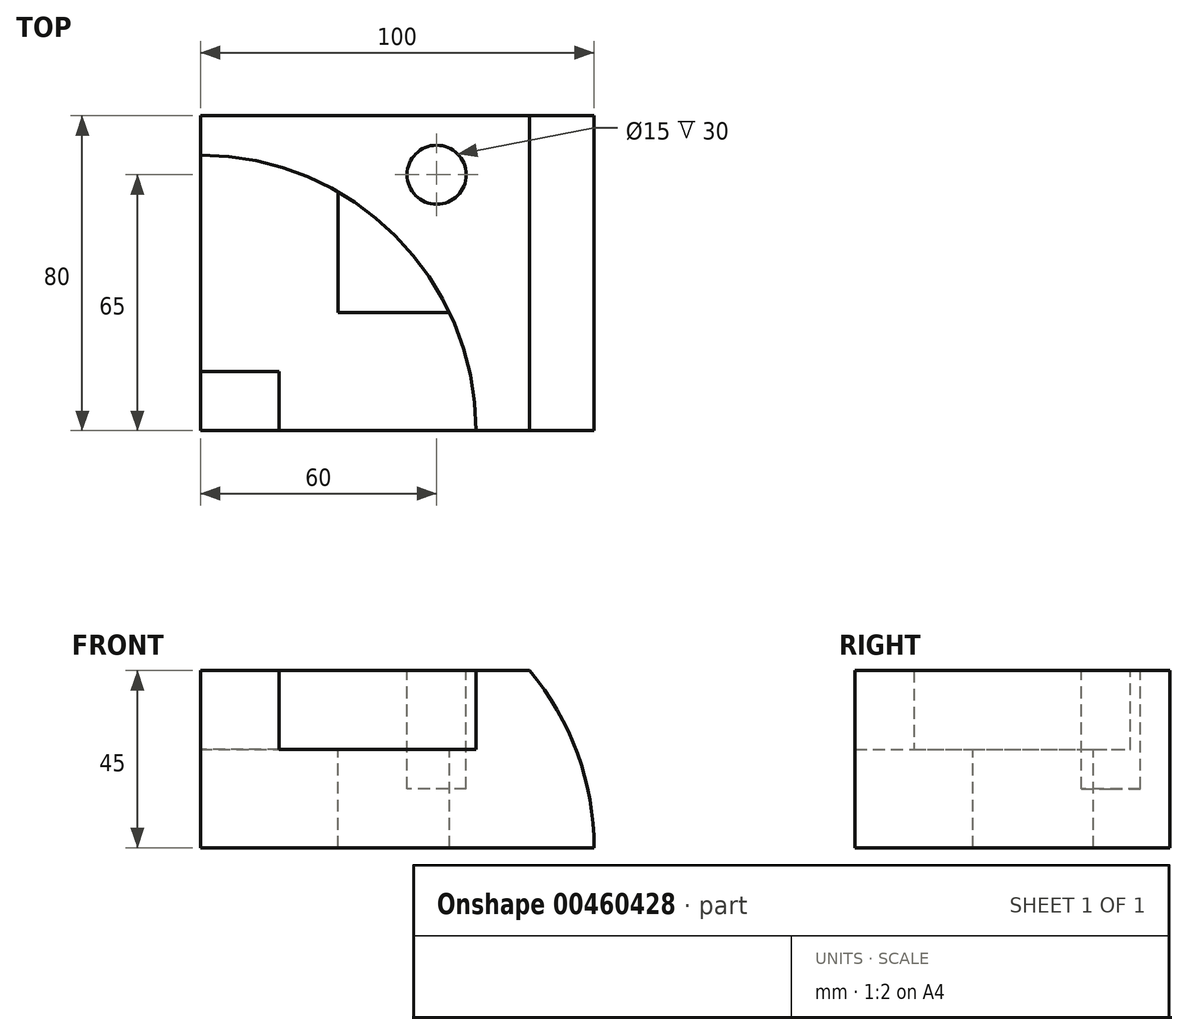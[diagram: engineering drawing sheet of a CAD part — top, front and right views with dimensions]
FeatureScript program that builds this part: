
annotation { "Feature Type Name" : "Feature", "Feature Type Description" : "" }
export const myFeature = defineFeature(function(context is Context, id is Id, definition is map)
    precondition{}
    {
        {
            var Q0;
            Q0=qCreatedBy(makeId("Front.planeOp"),FACE);
            var sketch = newSketch(context, id + "F0", { "sketchPlane" : qUnion([Q0])});
            skLineSegment(sketch, "E0.bottom", {"start": v(0, 0) * mm, "end": v(100, 0) * mm});
            skLineSegment(sketch, "E0.top", {"start": v(0, 45) * mm, "end": v(100, 45) * mm});
            skLineSegment(sketch, "E0.left", {"start": v(0, 0) * mm, "end": v(0, 45) * mm});
            skLineSegment(sketch, "E0.right", {"start": v(100, 0) * mm, "end": v(100, 45) * mm});
            skSolve(sketch);
        }
        {
            var Q0;
            Q0=makeQuery(id+"F0.imprint","IMPRINT",FACE,{"disambiguationData":[TD([[makeQuery(id+"F0.imprint","IMPRINT",EDGE,{"derivedFrom":sQuery(id+"F0.wireOp",EDGE,"E0.bottom")}),1.0]])]});
            extrude(context, id + "F1", {"entities" : qUnion([Q0]), "depth" : 80 * mm});
        }
        {
            var Q0;
            Q0=makeQuery(id+"F1.opExtrude","SWEPT_FACE",FACE,{"disambiguationData":[OSD([sQuery(id+"F0.wireOp",EDGE,"E0.top")])]});
            var sketch = newSketch(context, id + "F2", { "sketchPlane" : qUnion([Q0])});
            skCircle(sketch, "E1", {"center": v(0, -80) * mm, "radius": 70 * mm});
            skSolve(sketch);
        }
        {
            var Q0;
            {var subQ0=sQuery(id+"F2.wireOp",EDGE,"E1");var subQ1=sQuery(id+"F0.wireOp",EDGE,"E0.top");var subQ4=makeQuery(id+"F1.opExtrude","CAP_EDGE",EDGE,{"disambiguationData":[OSD([subQ1])],"isStart":false});var subQ5=makeQuery(id+"F2.imprint","INTERSECT",VERTEX,{"derivedFrom":[subQ4,subQ0]});Q0=makeQuery(id+"F2.imprint","IMPRINT",FACE,{"disambiguationData":[TD([[makeQuery(id+"F2.imprint","IMPRINT",EDGE,{"disambiguationData":[TD([[subQ5,-1.0]])],"derivedFrom":subQ0}),1.0]])]});}
            extrude(context, id + "F3", {"entities" : qUnion([Q0]), "operationType" : NewBodyOperationType.REMOVE, "oppositeDirection" : true, "depth" : 20 * mm});
        }
        {
            var Q0;
            Q0=makeQuery(id+"F1.opExtrude","SWEPT_FACE",FACE,{"disambiguationData":[OSD([sQuery(id+"F0.wireOp",EDGE,"E0.top")])]});
            var sketch = newSketch(context, id + "F4", { "sketchPlane" : qUnion([Q0])});
            skLineSegment(sketch, "E2", {"start": v(0, 0) * mm, "end": v(60, 0) * mm});
            skLineSegment(sketch, "E3", {"start": v(60, 0) * mm, "end": v(60, -15) * mm});
            skCircle(sketch, "E4", {"center": v(60, -15) * mm, "radius": 7.5 * mm});
            skSolve(sketch);
        }
        {
            var Q0;
            Q0=makeQuery(id+"F4.imprint","IMPRINT",FACE,{"disambiguationData":[TD([[makeQuery(id+"F4.imprint","IMPRINT",EDGE,{"derivedFrom":sQuery(id+"F4.wireOp",EDGE,"E4")}),1.0]])]});
            extrude(context, id + "F5", {"entities" : qUnion([Q0]), "operationType" : NewBodyOperationType.REMOVE, "oppositeDirection" : true, "depth" : 30 * mm});
        }
        {
            var Q0;
            Q0=makeQuery(id+"F3.boolean.opBoolean","COPY",FACE,{"derivedFrom":makeQuery(id+"F3.opExtrude","CAP_FACE",FACE,{"disambiguationData":[OSD([sQuery(id+"F0.wireOp",EDGE,"E0.top"),sQuery(id+"F0.wireOp",EDGE,"E0.left"),sQuery(id+"F2.wireOp",EDGE,"E1")])],"isStart":false})});
            var sketch = newSketch(context, id + "F6", { "sketchPlane" : qUnion([Q0])});
            skLineSegment(sketch, "E5.bottom", {"start": v(0, -80) * mm, "end": v(20, -80) * mm});
            skLineSegment(sketch, "E5.top", {"start": v(0, -65) * mm, "end": v(20, -65) * mm});
            skLineSegment(sketch, "E5.left", {"start": v(0, -80) * mm, "end": v(0, -65) * mm});
            skLineSegment(sketch, "E5.right", {"start": v(20, -80) * mm, "end": v(20, -65) * mm});
            skSolve(sketch);
        }
        {
            var Q0;
            Q0=makeQuery(id+"F6.imprint","IMPRINT",FACE,{"disambiguationData":[TD([[makeQuery(id+"F6.imprint","IMPRINT",EDGE,{"derivedFrom":sQuery(id+"F6.wireOp",EDGE,"E5.bottom")}),1.0]])]});
            extrude(context, id + "F7", {"entities" : qUnion([Q0]), "operationType" : NewBodyOperationType.ADD, "depth" : 20 * mm});
        }
        {
            var Q0;
            Q0=makeQuery(id+"F3.boolean.opBoolean","COPY",FACE,{"derivedFrom":makeQuery(id+"F3.opExtrude","CAP_FACE",FACE,{"disambiguationData":[OSD([sQuery(id+"F0.wireOp",EDGE,"E0.top"),sQuery(id+"F0.wireOp",EDGE,"E0.left"),sQuery(id+"F2.wireOp",EDGE,"E1")])],"isStart":false})});
            var sketch = newSketch(context, id + "F8", { "sketchPlane" : qUnion([Q0])});
            skLineSegment(sketch, "E6", {"start": v(0, -80) * mm, "end": v(35, -80) * mm});
            skLineSegment(sketch, "E7", {"start": v(0, -80) * mm, "end": v(0, -50) * mm});
            skLineSegment(sketch, "E8", {"start": v(0, -50) * mm, "end": v(35, -50) * mm});
            skLineSegment(sketch, "E9", {"start": v(35, -50) * mm, "end": v(35, -80) * mm});
            skLineSegment(sketch, "E10", {"start": v(35, -50) * mm, "end": v(63.25, -50) * mm});
            skLineSegment(sketch, "E11", {"start": v(35, -50) * mm, "end": v(35, -19.38) * mm});
            skSolve(sketch);
        }
        {
            var Q0;
            {var subQ0=sQuery(id+"F8.wireOp",EDGE,"E10");Q0=makeQuery(id+"F8.imprint","IMPRINT",FACE,{"disambiguationData":[TD([[makeQuery(id+"F8.imprint","IMPRINT",EDGE,{"derivedFrom":subQ0}),1.0]])]});}
            extrude(context, id + "F9", {"entities" : qUnion([Q0]), "operationType" : NewBodyOperationType.REMOVE, "endBound" : BoundingType.THROUGH_ALL, "oppositeDirection" : true, "depth" : 25 * mm});
        }
        {
            var Q0;
            Q0=makeQuery(id+"F7.boolean.opBoolean","MERGE",FACE,{"derivedFrom":[makeQuery(id+"F1.opExtrude","CAP_FACE",FACE,{"disambiguationData":[OSD([sQuery(id+"F0.wireOp",EDGE,"E0.bottom"),sQuery(id+"F0.wireOp",EDGE,"E0.top"),sQuery(id+"F0.wireOp",EDGE,"E0.left"),sQuery(id+"F0.wireOp",EDGE,"E0.right")])],"isStart":false}),makeQuery(id+"F7.opExtrude","SWEPT_FACE",FACE,{"disambiguationData":[OSD([sQuery(id+"F6.wireOp",EDGE,"E5.bottom")])]})]});
            var sketch = newSketch(context, id + "F10", { "sketchPlane" : qUnion([Q0])});
            skLineSegment(sketch, "E12", {"start": v(0, 0) * mm, "end": v(30, 0) * mm});
            skCircle(sketch, "E13", {"center": v(30, 0) * mm, "radius": 70 * mm});
            skSolve(sketch);
        }
        {
            var Q0;
            {var subQ1=makeQuery(id+"F1.opExtrude","CAP_EDGE",EDGE,{"disambiguationData":[OSD([sQuery(id+"F0.wireOp",EDGE,"E0.right")])],"isStart":false});Q0=makeQuery(id+"F10.imprint","IMPRINT",FACE,{"disambiguationData":[TD([[makeQuery(id+"F10.imprint","IMPRINT",EDGE,{"derivedFrom":subQ1}),1.0]])]});}
            extrude(context, id + "F11", {"entities" : qUnion([Q0]), "operationType" : NewBodyOperationType.REMOVE, "endBound" : BoundingType.THROUGH_ALL, "oppositeDirection" : true, "depth" : 25 * mm});
        }
    });
